# Revit family: Einschlaganker E und ES, gvz
name_source: partatom
category: HLS-Bauteile
revit_build: Autodesk Revit 2018 (Build: 20190510_1515(x64)
units: mm (PartAtom-declared; Revit-internal decimal feet)

## family parameters
Basisbauteil = Fläche
Beim Laden mit Abzugskörper schneiden = Nein
Bemaßung runder Anschluss = Durchmesser verwenden
Gemeinsam genutzt = Ja
Raumberechnungspunkt = Nein
Teiletyp = Normal

## types (8) — shared parameters
Firma = MEFA Befestigungs- und Montagesysteme GmbH
Material = Stahl
Mengeneinheit = St
Vorgabe-Ansicht = 1219 mm

## per-type parameters (varying)
| type | Artikelnummer | Bohrerdurchmesser | Bohrlochtiefe | D | EAN | Fabrikat | Gewicht | Gewicht pro Bauteil | Gewinde | Kurztext1 | Kurztext2 | Länge | Länge Gewinde | T | d1 | max. Einschraubtiefe | min. Einschraubtiefe | vpe |
| Einschlaganker E M 6x30, gvz | 210805005101 | 8 mm | 30 mm | 3 mm  [stored 0.00984252 ft] | 4043315010353 | MKT | 0.01 kg | 0.01 kg | M6 | Einschlaganker E | M6 x 30 | 13 mm | 13 mm | 30 mm  [stored 0.0984252 ft] | 4 mm  [stored 0.0131234 ft] | 13 mm | 7 mm | 100 St |
| Einschlaganker ES M 8x25, gvz | 210805125101 | 10 mm | 25 mm | 3 mm  [stored 0.00984252 ft] | 4250928457592 | MEFA | 0.01 kg | 0.01 kg | M8 | Einschlaganker ES | M8 x 25 | 12 mm  [stored 0.0393701 ft] | 12 mm  [stored 0.0393701 ft] | 25 mm  [stored 0.082021 ft] | 5 mm  [stored 0.0164042 ft] | 12 mm | 8 mm | 100 St |
| Einschlaganker ES M 8x30, gvz | 210805130101 | 10 mm | 30 mm | 3 mm  [stored 0.00984252 ft] | 4043315097675 | MEFA | 0.01 kg | 0.01 kg | M8 | Einschlaganker ES | M8 x 30 | 13 mm | 13 mm | 30 mm  [stored 0.0984252 ft] | 5 mm  [stored 0.0164042 ft] | 13 mm | 9 mm | 100 St |
| Einschlaganker ES M 8x40, gvz | 210805155101 | 10 mm | 40 mm | 3 mm  [stored 0.00984252 ft] | 4043315010780 | MEFA | 0.02 kg | 0.02 kg | M8 | Einschlaganker ES | M8 x 40 | 20 mm  [stored 0.0656168 ft] | 20 mm  [stored 0.0656168 ft] | 40 mm  [stored 0.131234 ft] | 5 mm  [stored 0.0164042 ft] | 20 mm | 9 mm | 100 St |
| Einschlaganker ES M10x25, gvz | 210805225101 | 12 mm | 25 mm | 4 mm  [stored 0.0131234 ft] | 4250928457608 | MEFA | 0.02 kg | 0.02 kg | M10 | Einschlaganker ES | M10 x 25 | 12 mm  [stored 0.0393701 ft] | 12 mm  [stored 0.0393701 ft] | 25 mm  [stored 0.082021 ft] | 6 mm  [stored 0.019685 ft] | 12 mm | 10 mm | 50 St |
| Einschlaganker ES M10x40, gvz | 210805240101 | 12 mm | 40 mm | 4 mm  [stored 0.0131234 ft] | 4043315097576 | MEFA | 0.02 kg | 0.02 kg | M10 | Einschlaganker ES | M10 x 40 | 15 mm  [stored 0.0492126 ft] | 15 mm  [stored 0.0492126 ft] | 40 mm  [stored 0.131234 ft] | 6 mm  [stored 0.019685 ft] | 15 mm | 11 mm | 50 St |
| Einschlaganker ES M12x50, gvz | 210805330101 | 15 mm | 50 mm | 5 mm  [stored 0.0164042 ft] | 4043315097682 | MEFA | 0.04 kg | 0.04 kg | M12 | Einschlaganker ES | M12 x 50 | 18 mm  [stored 0.0590551 ft] | 18 mm  [stored 0.0590551 ft] | 50 mm  [stored 0.164042 ft] | 8 mm  [stored 0.0262467 ft] | 18 mm | 13 mm | 50 St |
| Einschlaganker E M16x65, gvz | 210805500101 | 20 mm | 65 mm | 7 mm  [stored 0.0229659 ft] | 4043315011527 | MKT | 0.10 kg | 0.10 kg | M16 | Einschlaganker E | M16 x 65 | 23 mm  [stored 0.0754593 ft] | 23 mm  [stored 0.0754593 ft] | 65 mm  [stored 0.213255 ft] | 10 mm  [stored 0.0328084 ft] | 23 mm | 18 mm | 25 St |

note: [stored X ft] marks values corroborated as IEEE doubles in the binary element streams (Revit-internal decimal feet)
